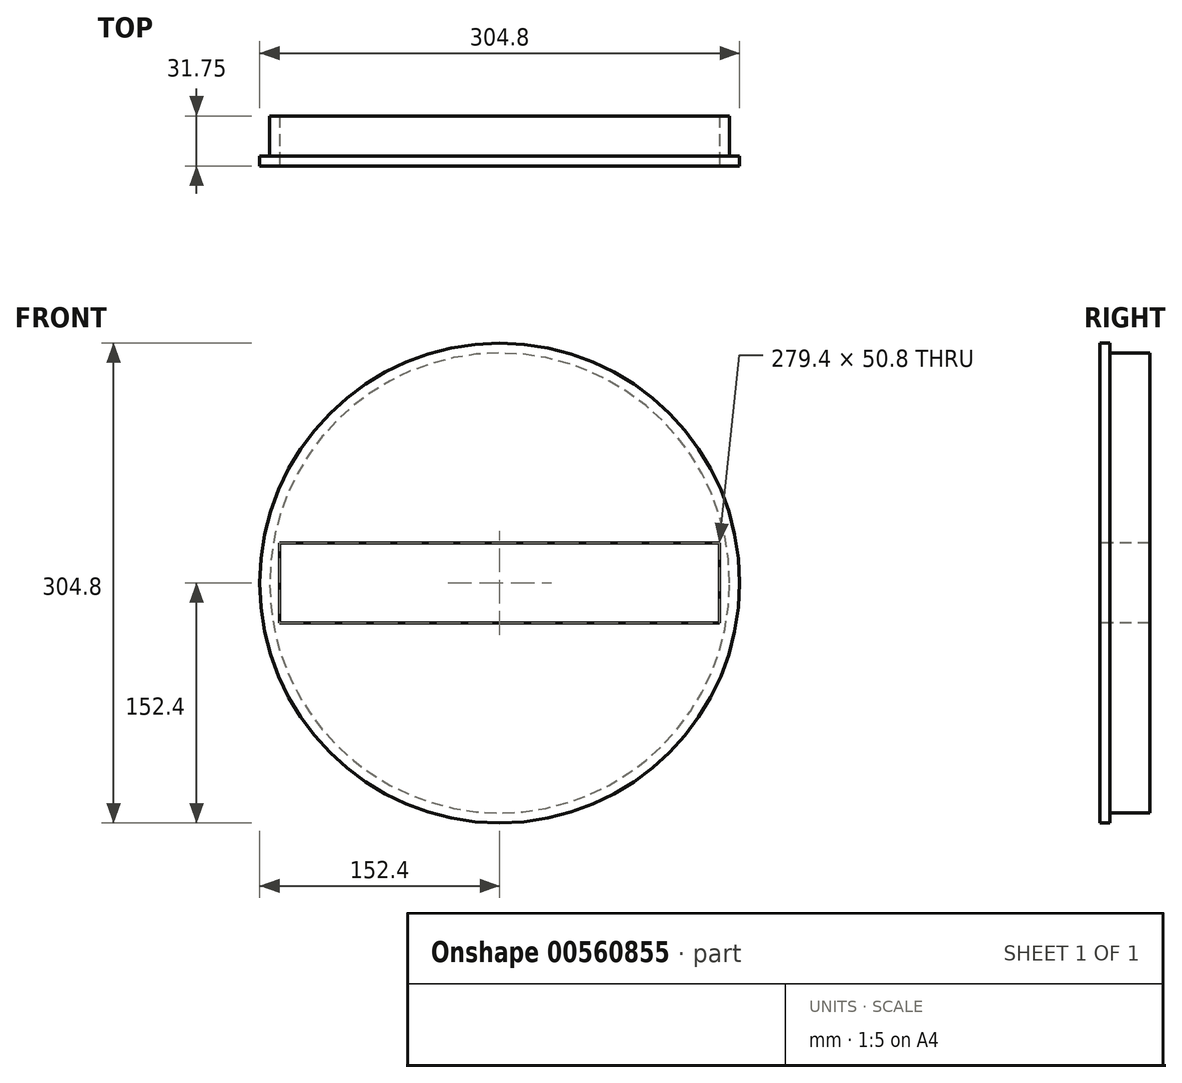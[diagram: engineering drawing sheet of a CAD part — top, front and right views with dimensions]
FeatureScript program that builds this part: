
annotation { "Feature Type Name" : "Feature", "Feature Type Description" : "" }
export const myFeature = defineFeature(function(context is Context, id is Id, definition is map)
    precondition{}
    {
        {
            var Q0;
            Q0=qCreatedBy(makeId("Right.planeOp"),FACE);
            var sketch = newSketch(context, id + "F0", { "sketchPlane" : qUnion([Q0])});
            skLineSegment(sketch, "E0", {"start": v(0, 0) * mm, "end": v(0, 152.4) * mm});
            skLineSegment(sketch, "E1", {"start": v(0, 152.4) * mm, "end": v(6.35, 152.4) * mm});
            skLineSegment(sketch, "E2", {"start": v(6.35, 152.4) * mm, "end": v(6.35, 146.05) * mm});
            skLineSegment(sketch, "E3", {"start": v(6.35, 146.05) * mm, "end": v(31.75, 146.05) * mm});
            skLineSegment(sketch, "E4", {"start": v(31.75, 146.05) * mm, "end": v(31.75, 0) * mm});
            skLineSegment(sketch, "E5", {"start": v(31.75, 0) * mm, "end": v(0, 0) * mm});
            skLineSegment(sketch, "E6", {"start": v(0, 0) * mm, "end": v(118.1, 0) * mm, "construction": true});
            skSolve(sketch);
        }
        {
            var Q0;
            Q0 = qSketchRegion(id + "F0", true);
            var Q1;
            Q1=sQuery(id+"F0.wireOp",EDGE,"E6");
            revolve(context, id + "F1", {"entities" : qUnion([Q0]), "axis" : qUnion([Q1]), "revolveType" : RevolveType.FULL});
        }
        {
            var Q0;
            Q0=makeQuery(id+"F1.opRevolve","SWEPT_FACE",FACE,{"disambiguationData":[OSD([sQuery(id+"F0.wireOp",EDGE,"E0")])]});
            var sketch = newSketch(context, id + "F2", { "sketchPlane" : qUnion([Q0])});
            skLineSegment(sketch, "E7.bottom", {"start": v(-139.7, 25.4) * mm, "end": v(139.7, 25.4) * mm});
            skLineSegment(sketch, "E7.top", {"start": v(-139.7, -25.4) * mm, "end": v(139.7, -25.4) * mm});
            skLineSegment(sketch, "E7.left", {"start": v(-139.7, 25.4) * mm, "end": v(-139.7, -25.4) * mm});
            skLineSegment(sketch, "E7.right", {"start": v(139.7, 25.4) * mm, "end": v(139.7, -25.4) * mm});
            skPoint(sketch, "E7.middle", {"position": v(0, 0) * mm});
            skSolve(sketch);
        }
        {
            var Q0;
            Q0 = qSketchRegion(id + "F2", true);
            extrude(context, id + "F3", {"entities" : qUnion([Q0]), "operationType" : NewBodyOperationType.REMOVE, "endBound" : BoundingType.THROUGH_ALL, "oppositeDirection" : true, "depth" : 25.4 * mm, "offsetDistance" : 25.4 * mm});
        }
    });
